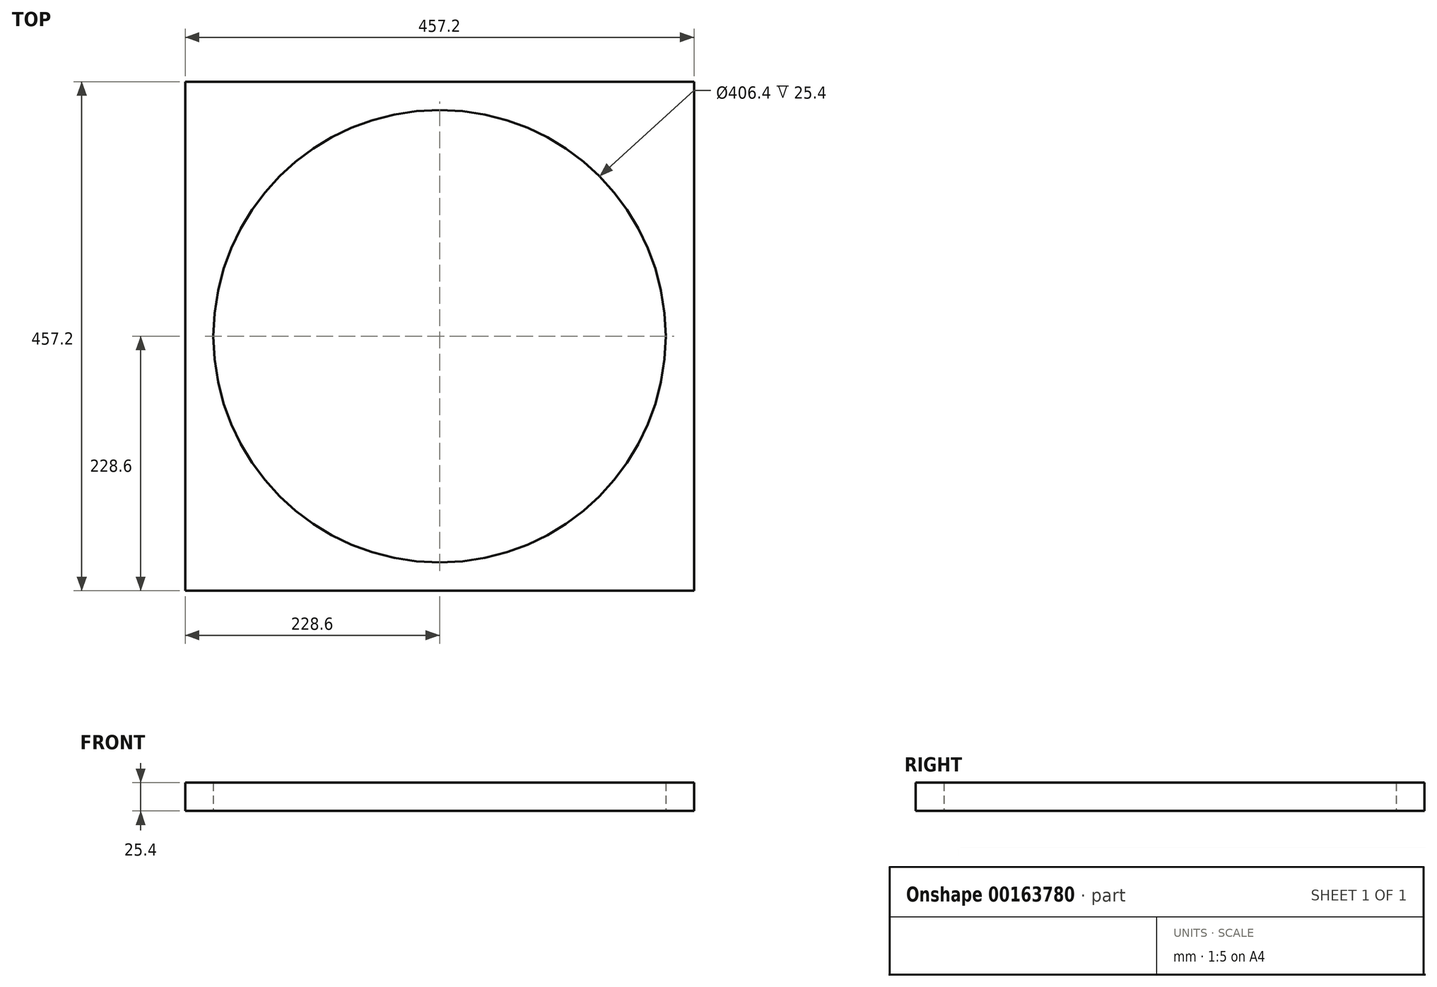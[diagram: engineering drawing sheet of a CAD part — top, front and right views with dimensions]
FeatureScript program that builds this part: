
annotation { "Feature Type Name" : "Feature", "Feature Type Description" : "" }
export const myFeature = defineFeature(function(context is Context, id is Id, definition is map)
    precondition{}
    {
        {
            var Q0;
            Q0=qCreatedBy(makeId("Top.planeOp"),FACE);
            var sketch = newSketch(context, id + "F0", { "sketchPlane" : qUnion([Q0])});
            skLineSegment(sketch, "E0.bottom", {"start": v(228.6, 228.6) * mm, "end": v(-228.6, 228.6) * mm});
            skLineSegment(sketch, "E0.top", {"start": v(228.6, -228.6) * mm, "end": v(-228.6, -228.6) * mm});
            skLineSegment(sketch, "E0.left", {"start": v(228.6, 228.6) * mm, "end": v(228.6, -228.6) * mm});
            skLineSegment(sketch, "E0.right", {"start": v(-228.6, 228.6) * mm, "end": v(-228.6, -228.6) * mm});
            skPoint(sketch, "E0.middle", {"position": v(0, 0) * mm});
            skCircle(sketch, "E1", {"center": v(0, 0) * mm, "radius": 203.2 * mm});
            skSolve(sketch);
        }
        {
            var Q0;
            Q0 = qSketchRegion(id + "F0", true);
            extrude(context, id + "F1", {"entities" : qUnion([Q0]), "depth" : 25.4 * mm});
        }
    });
